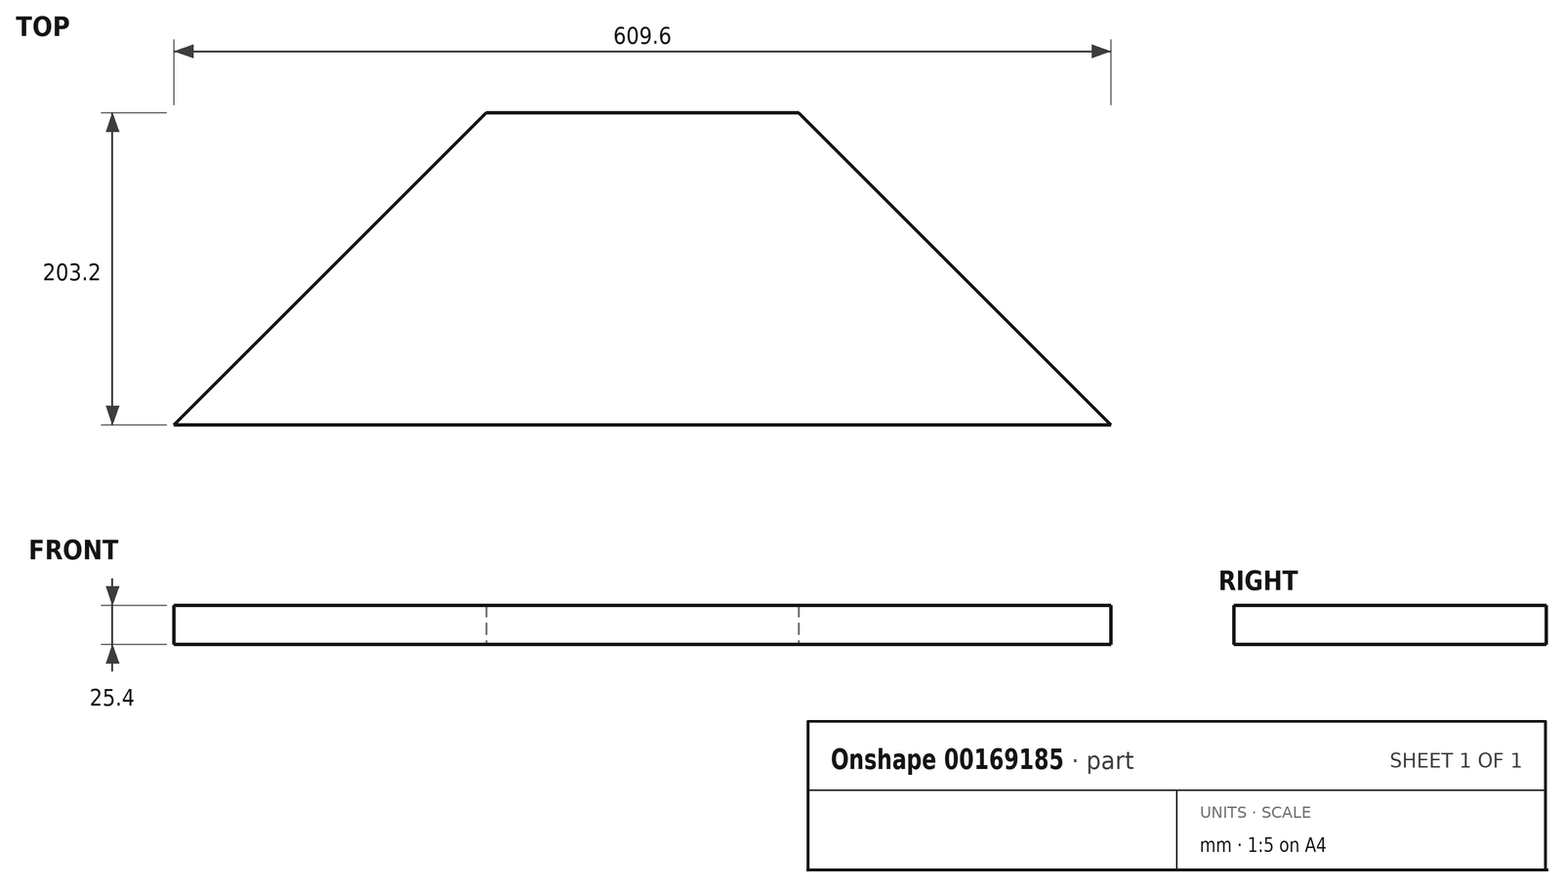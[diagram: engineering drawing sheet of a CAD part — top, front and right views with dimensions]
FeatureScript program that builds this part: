
annotation { "Feature Type Name" : "Feature", "Feature Type Description" : "" }
export const myFeature = defineFeature(function(context is Context, id is Id, definition is map)
    precondition{}
    {
        {
            var Q0;
            Q0=qCreatedBy(makeId("Top.planeOp"),FACE);
            var sketch = newSketch(context, id + "F0", { "sketchPlane" : qUnion([Q0])});
            skLineSegment(sketch, "E0", {"start": v(609.6, 0) * mm, "end": v(0, 0) * mm});
            skLineSegment(sketch, "E1", {"start": v(609.6, 0) * mm, "end": v(406.4, 203.2) * mm});
            skLineSegment(sketch, "E2", {"start": v(203.2, 203.2) * mm, "end": v(0, 0) * mm});
            skLineSegment(sketch, "E3", {"start": v(203.2, 203.2) * mm, "end": v(406.4, 203.2) * mm});
            skSolve(sketch);
        }
        {
            var Q0;
            Q0=makeQuery(id+"F0.imprint","IMPRINT",FACE,{"disambiguationData":[TD([[makeQuery(id+"F0.imprint","IMPRINT",EDGE,{"derivedFrom":sQuery(id+"F0.wireOp",EDGE,"E0")}),-1.0]])]});
            extrude(context, id + "F1", {"entities" : qUnion([Q0]), "depth" : 25.4 * mm});
        }
    });
